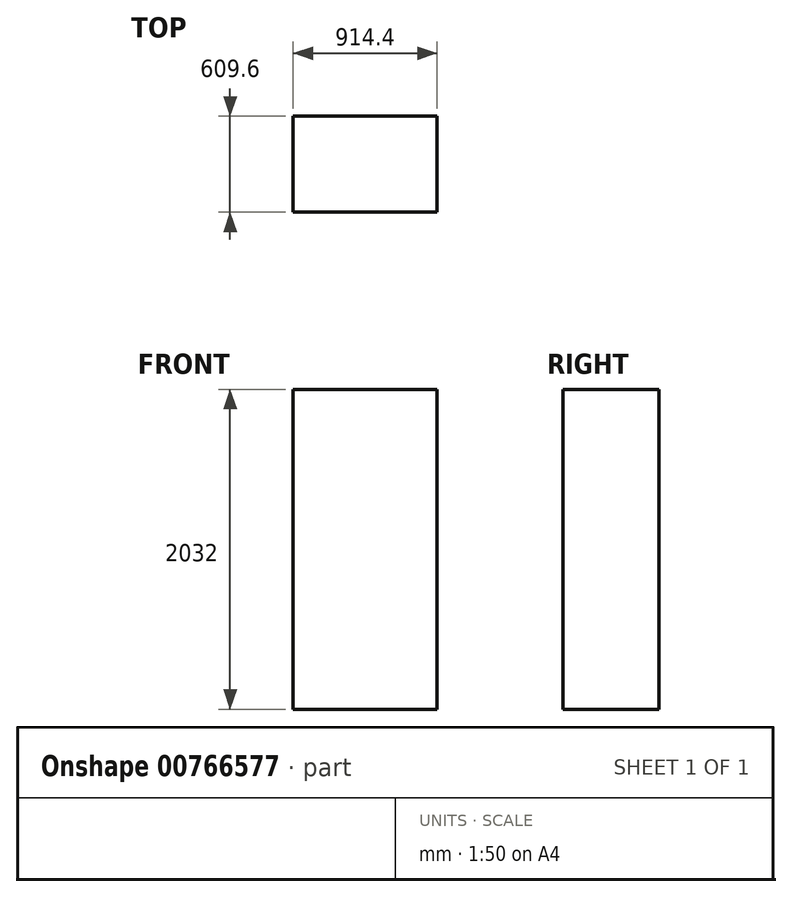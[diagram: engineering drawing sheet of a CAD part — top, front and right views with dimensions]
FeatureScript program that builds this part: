
annotation { "Feature Type Name" : "Feature", "Feature Type Description" : "" }
export const myFeature = defineFeature(function(context is Context, id is Id, definition is map)
    precondition{}
    {
        {
            var Q0;
            Q0=qCreatedBy(makeId("Top.planeOp"),FACE);
            var sketch = newSketch(context, id + "F0", { "sketchPlane" : qUnion([Q0])});
            skLineSegment(sketch, "E0.bottom", {"start": v(-457.2, 304.8) * mm, "end": v(457.2, 304.8) * mm});
            skLineSegment(sketch, "E0.top", {"start": v(-457.2, -304.8) * mm, "end": v(457.2, -304.8) * mm});
            skLineSegment(sketch, "E0.left", {"start": v(-457.2, 304.8) * mm, "end": v(-457.2, -304.8) * mm});
            skLineSegment(sketch, "E0.right", {"start": v(457.2, 304.8) * mm, "end": v(457.2, -304.8) * mm});
            skLineSegment(sketch, "E1", {"start": v(-457.2, 304.8) * mm, "end": v(457.2, -304.8) * mm, "construction": true});
            skSolve(sketch);
        }
        {
            var Q0;
            Q0 = qSketchRegion(id + "F0", true);
            extrude(context, id + "F1", {"entities" : qUnion([Q0]), "depth" : 2032 * mm, "offsetDistance" : 25.4 * mm});
        }
    });
